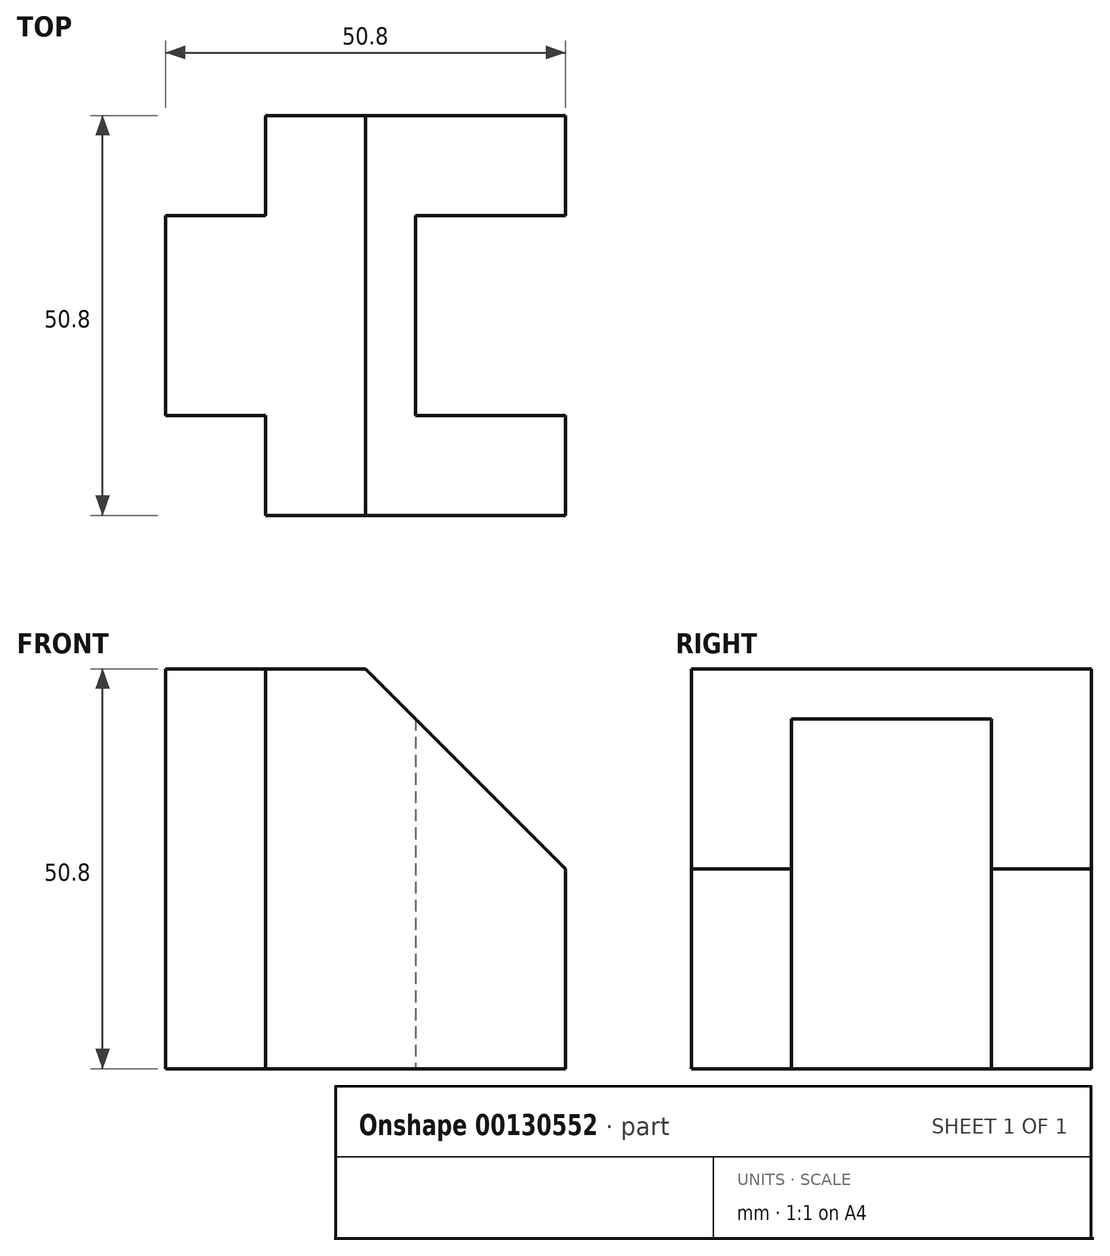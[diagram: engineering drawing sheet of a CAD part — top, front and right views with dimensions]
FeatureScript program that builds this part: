
annotation { "Feature Type Name" : "Feature", "Feature Type Description" : "" }
export const myFeature = defineFeature(function(context is Context, id is Id, definition is map)
    precondition{}
    {
        {
            var Q0;
            Q0=qCreatedBy(makeId("Top.planeOp"),FACE);
            var sketch = newSketch(context, id + "F0", { "sketchPlane" : qUnion([Q0])});
            skLineSegment(sketch, "E0", {"start": v(0, 0) * mm, "end": v(38.1, 0) * mm});
            skLineSegment(sketch, "E1", {"start": v(38.1, 0) * mm, "end": v(38.1, -12.7) * mm});
            skLineSegment(sketch, "E2", {"start": v(38.1, -12.7) * mm, "end": v(19.05, -12.7) * mm});
            skLineSegment(sketch, "E3", {"start": v(19.05, -12.7) * mm, "end": v(19.05, -38.1) * mm});
            skLineSegment(sketch, "E4", {"start": v(19.05, -38.1) * mm, "end": v(38.1, -38.1) * mm});
            skLineSegment(sketch, "E5", {"start": v(38.1, -38.1) * mm, "end": v(38.1, -50.8) * mm});
            skLineSegment(sketch, "E6", {"start": v(38.1, -50.8) * mm, "end": v(0, -50.8) * mm});
            skLineSegment(sketch, "E7", {"start": v(0, -50.8) * mm, "end": v(0, -38.1) * mm});
            skLineSegment(sketch, "E8", {"start": v(0, -38.1) * mm, "end": v(-12.7, -38.1) * mm});
            skLineSegment(sketch, "E9", {"start": v(-12.7, -38.1) * mm, "end": v(-12.7, -12.7) * mm});
            skLineSegment(sketch, "E10", {"start": v(-12.7, -12.7) * mm, "end": v(0, -12.7) * mm});
            skLineSegment(sketch, "E11", {"start": v(0, -12.7) * mm, "end": v(0, 0) * mm});
            skSolve(sketch);
        }
        {
            var Q0;
            Q0 = qSketchRegion(id + "F0", true);
            extrude(context, id + "F1", {"entities" : qUnion([Q0]), "depth" : 50.8 * mm});
        }
        {
            var Q0;
            Q0=makeQuery(id+"F1.opExtrude","SWEPT_FACE",FACE,{"disambiguationData":[OSD([sQuery(id+"F0.wireOp",EDGE,"E6")])]});
            var sketch = newSketch(context, id + "F2", { "sketchPlane" : qUnion([Q0])});
            skLineSegment(sketch, "E12", {"start": v(38.1, 50.8) * mm, "end": v(12.7, 50.8) * mm});
            skLineSegment(sketch, "E13", {"start": v(12.7, 50.8) * mm, "end": v(38.1, 25.4) * mm});
            skLineSegment(sketch, "E14", {"start": v(38.1, 25.4) * mm, "end": v(38.1, 50.8) * mm});
            skSolve(sketch);
        }
        {
            var Q0;
            Q0 = qSketchRegion(id + "F2", true);
            var Q1;
            Q1=makeQuery(id+"F1.opExtrude","SWEPT_FACE",FACE,{"disambiguationData":[OSD([sQuery(id+"F0.wireOp",EDGE,"E0")])]});
            extrude(context, id + "F3", {"entities" : qUnion([Q0]), "operationType" : NewBodyOperationType.REMOVE, "endBound" : BoundingType.UP_TO_SURFACE, "oppositeDirection" : true, "endBoundEntityFace" : qUnion([Q1]), "depth" : 25.4 * mm});
        }
    });
